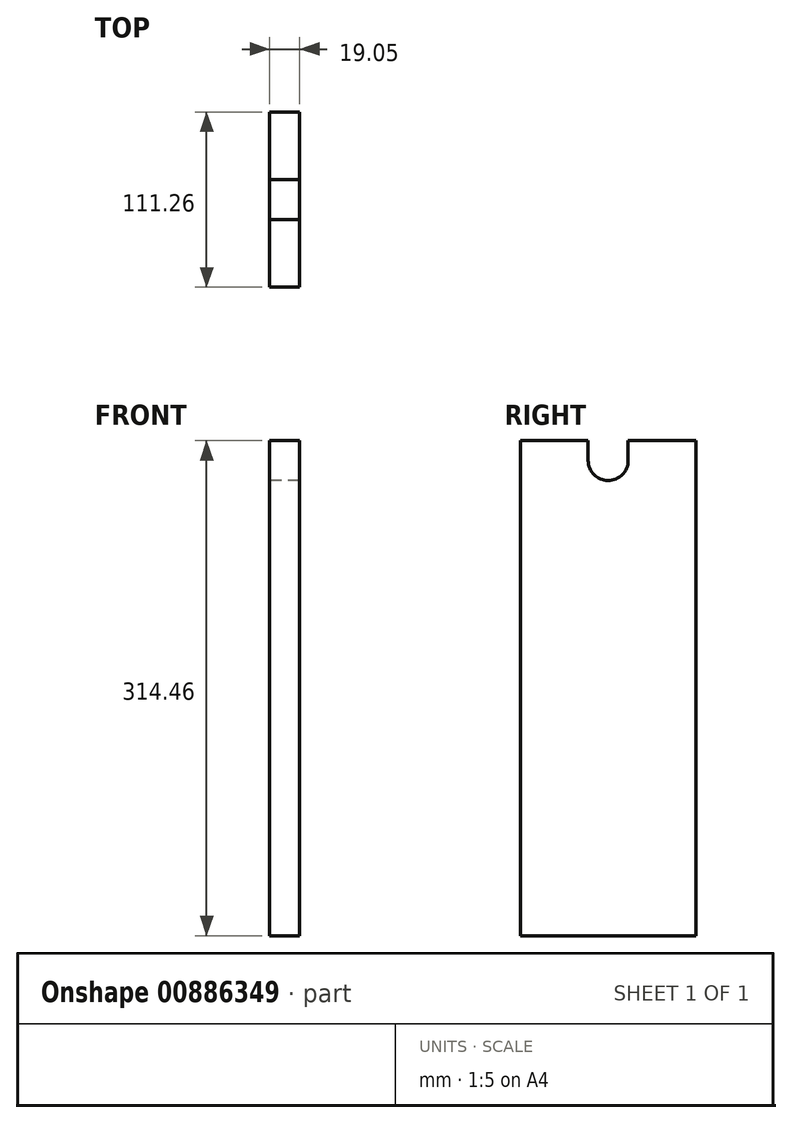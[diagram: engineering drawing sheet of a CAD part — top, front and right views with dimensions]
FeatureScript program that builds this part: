
annotation { "Feature Type Name" : "Feature", "Feature Type Description" : "" }
export const myFeature = defineFeature(function(context is Context, id is Id, definition is map)
    precondition{}
    {
        {
            var Q0;
            Q0=qCreatedBy(makeId("Right.planeOp"),FACE);
            var sketch = newSketch(context, id + "F0", { "sketchPlane" : qUnion([Q0])});
            skLineSegment(sketch, "E0.bottom", {"start": v(55.63, 157.23) * mm, "end": v(-55.63, 157.23) * mm});
            skLineSegment(sketch, "E0.top", {"start": v(55.63, -157.23) * mm, "end": v(-55.63, -157.23) * mm});
            skLineSegment(sketch, "E0.left", {"start": v(55.63, 157.23) * mm, "end": v(55.63, -157.23) * mm});
            skLineSegment(sketch, "E0.right", {"start": v(-55.63, 157.23) * mm, "end": v(-55.63, -157.23) * mm});
            skPoint(sketch, "E0.middle", {"position": v(0, 0) * mm});
            skLineSegment(sketch, "E1", {"start": v(0, 157.23) * mm, "end": v(0, 144.53) * mm});
            skCircle(sketch, "E2", {"center": v(0, 144.53) * mm, "radius": 12.7 * mm});
            skLineSegment(sketch, "E3", {"start": v(0, 144.53) * mm, "end": v(-12.7, 144.53) * mm});
            skLineSegment(sketch, "E4", {"start": v(-12.7, 144.53) * mm, "end": v(-12.7, 157.23) * mm});
            skLineSegment(sketch, "E5", {"start": v(0, 144.53) * mm, "end": v(12.7, 144.53) * mm});
            skLineSegment(sketch, "E6", {"start": v(12.7, 144.53) * mm, "end": v(12.7, 157.23) * mm});
            skSolve(sketch);
        }
        {
            var Q0;
            Q0=makeQuery(id+"F0.imprint","IMPRINT",FACE,{"disambiguationData":[TD([[makeQuery(id+"F0.imprint","IMPRINT",EDGE,{"derivedFrom":sQuery(id+"F0.wireOp",EDGE,"E0.top")}),-1.0]])]});
            extrude(context, id + "F1", {"entities" : qUnion([Q0]), "depth" : 19.05 * mm, "offsetDistance" : 25.4 * mm});
        }
    });
